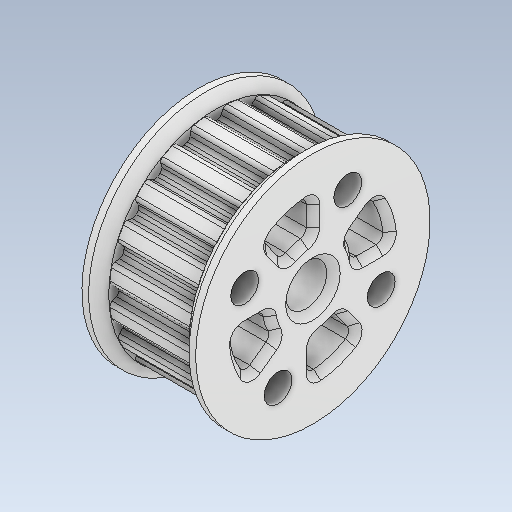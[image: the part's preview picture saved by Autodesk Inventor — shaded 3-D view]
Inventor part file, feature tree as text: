
AUTODESK INVENTOR PART (.ipt)
format: ipt  version: 2020 (Build 240168000, 168)  size: 1,363,456 bytes
history: native  units: mm
features: sketch x9, extrude x8, thicken_offset x8, projected_geometry x7, chamfer x4, pattern_circular x2, plane x1, fillet x1, hole x1, other x1
ambient origin geometry x8: Origin, YZ Plane, XZ Plane, XY Plane, X Axis, Y Axis, Z Axis, Center Point
bodies: Solid1 (feature_tree)
feature tree (42):
  extrude  "Extrusion1"  Depth=10.0mm TaperAngle=0.0deg
  plane  "Work Plane1"
  extrude  "Extrusion2"  Depth=50.0mm
  extrude  "Extrusion3"  Depth=10.0mm TaperAngle=0.0deg
  thicken_offset  "Thicken1"
  extrude  "Extrusion4"  Depth=9.0mm
  pattern_circular  "Circular Pattern1"  Count=4  [1 undecoded]
  extrude  "Extrusion5"  Depth=10.0mm TaperAngle=0.0deg
  extrude  "Extrusion6"  Depth=2.0mm TaperAngle=0.0deg
  extrude  "Extrusion7"  Depth=2.0mm TaperAngle=0.0deg
  extrude  "Extrusion8"  Depth=2.0mm
  thicken_offset  "Thicken2"
  fillet  "Fillet1"  Radius=25.0mm
  pattern_circular  "Circular Pattern2"  [2 undecoded]
  thicken_offset  "Thicken3"
  thicken_offset  "Thicken4"
  hole  "Hole1"  [1 undecoded]
  chamfer  "Chamfer2"  Distance=1.0mm
  thicken_offset  "Thicken5"
  thicken_offset  "Thicken6"
  chamfer  "Chamfer3"  Distance=1.0mm
  thicken_offset  "Thicken7"
  thicken_offset  "Thicken8"
  chamfer  "Chamfer4"  Distance=1.0mm
  chamfer  "Chamfer5"  Distance=40.0mm
  sketch  "Sketch1"  dims[d0=50.0mm d1=10.0mm d2=0.0mm]
  sketch  "Sketch2"  dims[d3=-1.0mm d4=50.0mm]
  sketch  "Sketch3"  dims[d5=10.0mm d6=0.0mm d7=10.0mm d8=0.0mm]
  projected_geometry  "Projected Loop1"
  sketch  "Sketch4"  dims[d9=9.0mm d10=9.0mm]
  projected_geometry  "Projected Loop2"
  sketch  "Sketch5"  dims[d11=11.45mm]
  projected_geometry  "Projected Loop3"
  sketch  "Sketch6"  dims[d12=4.0mm]
  projected_geometry  "Projected Loop4"
  sketch  "Sketch7"  dims[d13=10.0mm d14=0.0mm d15=40.0mm d16=62.831853mm]
  projected_geometry  "Projected Loop5"
  sketch  "Sketch8"  dims[d18=6.15mm d19=10.0mm d20=0.0mm]
  projected_geometry  "Projected Loop6"
  sketch  "Sketch9"  dims[d21=36.0mm d22=3.0mm d23=0.0mm d24=3.0mm d25=0.0mm d26=13.0mm d27=25.0mm d28=4.7mm d29=16.0mm d30=0.0mm d31=1.0mm d32=1.0mm d33=1.0mm d34=40.0mm d35=62.831853mm d40=1.0mm d41=1.0mm d42=1.0mm d43=1.0mm d44=4.15mm d45=6.0mm d46=4.0mm d47=2.0mm d48=90.0deg d49=20.0mm d50=0.0mm d51=1.0mm d52=2.0mm d53=45.0deg d54=0.5mm d55=0.7mm d56=0.5mm d57=0.7mm d58=1.0mm d59=2.0mm d60=45.0deg d61=0.5mm d62=1.0mm d63=0.5mm d64=1.0mm d65=1.5mm d66=2.0mm d67=45.0deg d68=1.5mm d69=2.0mm d70=45.0deg]
  projected_geometry  "Projected Loop7"
  other  "_ATP20XL025-A-C10_b"
note: 4 required parameter values undecoded (feature->parameter linkage not recoverable at this tier; creation-order binding heuristic only, values carry confidence <= 0.55)
